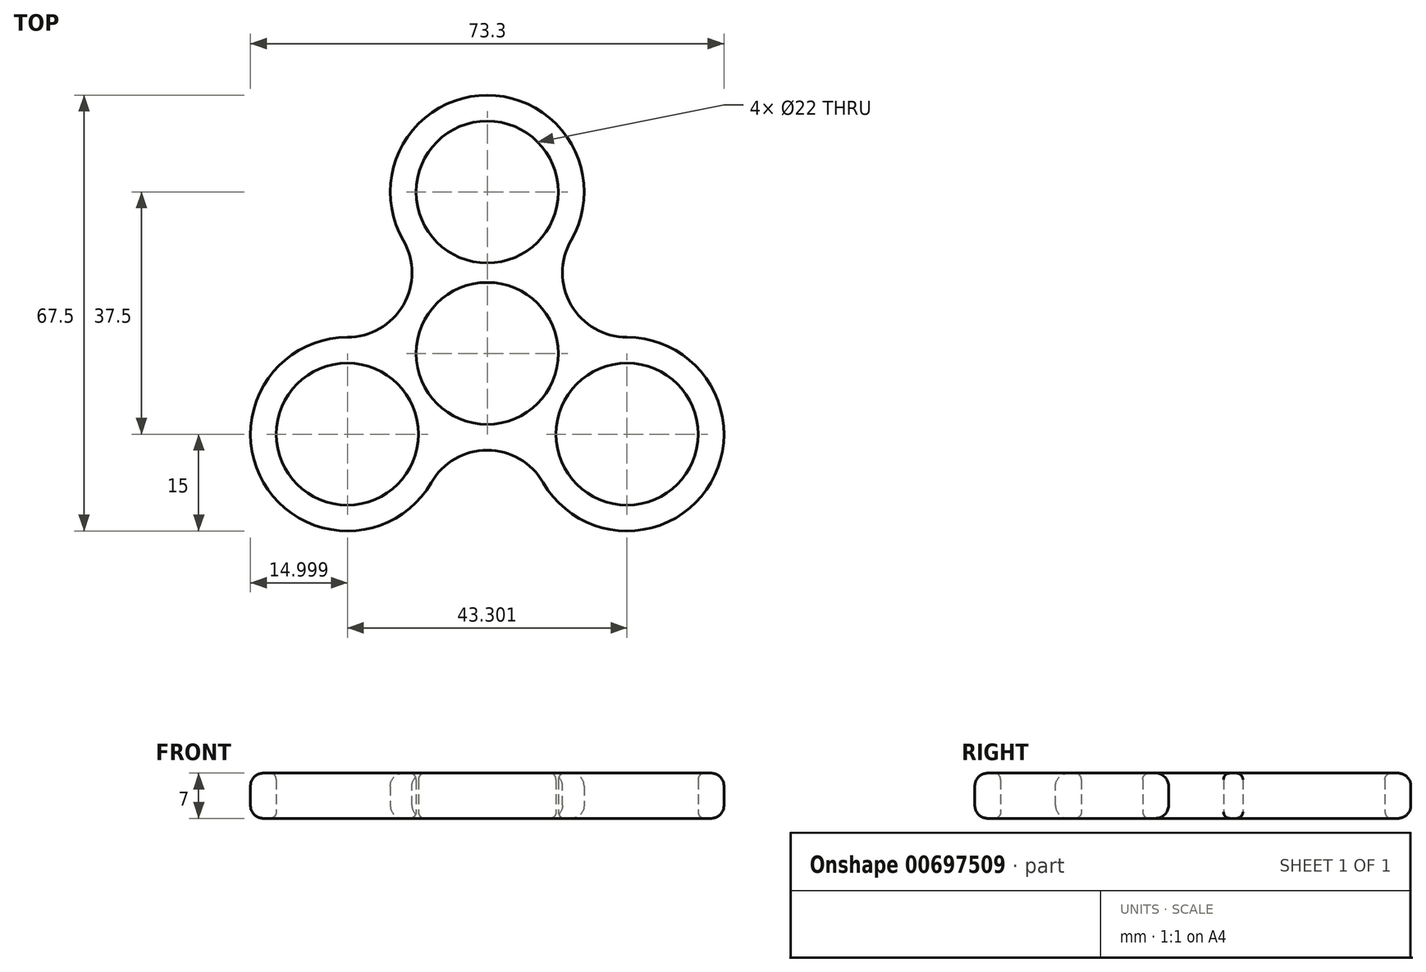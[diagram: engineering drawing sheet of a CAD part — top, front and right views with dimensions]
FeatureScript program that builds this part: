
annotation { "Feature Type Name" : "Feature", "Feature Type Description" : "" }
export const myFeature = defineFeature(function(context is Context, id is Id, definition is map)
    precondition{}
    {
        {
            var Q0;
            Q0=qCreatedBy(makeId("Top.planeOp"),FACE);
            var sketch = newSketch(context, id + "F0", { "sketchPlane" : qUnion([Q0])});
            skCircle(sketch, "E0", {"center": v(0, 0) * mm, "radius": 11 * mm});
            skArc(sketch, "E1", {"start": v(-8.3, 12.5) * mm, "mid": v(-13, 7.5) * mm, "end": v(-14.97, 0.93) * mm});
            skCircle(sketch, "E2", {"center": v(0, 0) * mm, "radius": 25 * mm, "construction": true});
            skLineSegment(sketch, "E3", {"start": v(0, 0) * mm, "end": v(0, 25) * mm, "construction": true});
            skLineSegment(sketch, "E4", {"start": v(0, 0) * mm, "end": v(21.65, -12.5) * mm, "construction": true});
            skLineSegment(sketch, "E5", {"start": v(0, 0) * mm, "end": v(-21.65, -12.5) * mm, "construction": true});
            skCircle(sketch, "E6", {"center": v(0, 25) * mm, "radius": 11 * mm});
            skCircle(sketch, "E7", {"center": v(-21.65, -12.5) * mm, "radius": 11 * mm});
            skArc(sketch, "E8", {"start": v(-14.97, 0.93) * mm, "mid": v(-34.64, -20) * mm, "end": v(-6.68, -13.43) * mm});
            skCircle(sketch, "E9", {"center": v(21.65, -12.5) * mm, "radius": 11 * mm});
            skArc(sketch, "E10", {"start": v(6.68, -13.43) * mm, "mid": v(34.64, -20) * mm, "end": v(14.97, 0.93) * mm});
            skArc(sketch, "E11.trimOffspring", {"start": v(8.3, 12.5) * mm, "mid": v(0, 40) * mm, "end": v(-8.3, 12.5) * mm});
            skArc(sketch, "E12.trimOffspring", {"start": v(-6.68, -13.43) * mm, "mid": v(0, -15) * mm, "end": v(6.68, -13.43) * mm});
            skArc(sketch, "E13.trimOffspring", {"start": v(14.97, 0.93) * mm, "mid": v(13, 7.5) * mm, "end": v(8.3, 12.5) * mm});
            skSolve(sketch);
        }
        {
            var Q0;
            Q0=makeQuery(id+"F0.imprint","IMPRINT",FACE,{"disambiguationData":[TD([[makeQuery(id+"F0.imprint","IMPRINT",EDGE,{"derivedFrom":sQuery(id+"F0.wireOp",EDGE,"E0")}),-1.0]])]});
            extrude(context, id + "F1", {"entities" : qUnion([Q0]), "depth" : 7 * mm, "offsetDistance" : 25 * mm});
        }
        {
            var Q0;
            Q0=makeQuery(id+"F1.opExtrude","SWEPT_EDGE",EDGE,{"disambiguationData":[OSD([sQuery(id+"F0.wireOp",EDGE,"E11.trimOffspring"),sQuery(id+"F0.wireOp",EDGE,"E13.trimOffspring")])]});
            var Q1;
            Q1=makeQuery(id+"F1.opExtrude","SWEPT_EDGE",EDGE,{"disambiguationData":[OSD([sQuery(id+"F0.wireOp",EDGE,"E10"),sQuery(id+"F0.wireOp",EDGE,"E13.trimOffspring")])]});
            var Q2;
            Q2=makeQuery(id+"F1.opExtrude","SWEPT_EDGE",EDGE,{"disambiguationData":[OSD([sQuery(id+"F0.wireOp",EDGE,"E8"),sQuery(id+"F0.wireOp",EDGE,"E12.trimOffspring")])]});
            var Q3;
            Q3=makeQuery(id+"F1.opExtrude","SWEPT_EDGE",EDGE,{"disambiguationData":[OSD([sQuery(id+"F0.wireOp",EDGE,"E10"),sQuery(id+"F0.wireOp",EDGE,"E12.trimOffspring")])]});
            var Q4;
            Q4=makeQuery(id+"F1.opExtrude","SWEPT_EDGE",EDGE,{"disambiguationData":[OSD([sQuery(id+"F0.wireOp",EDGE,"E1"),sQuery(id+"F0.wireOp",EDGE,"E11.trimOffspring")])]});
            var Q5;
            Q5=makeQuery(id+"F1.opExtrude","SWEPT_EDGE",EDGE,{"disambiguationData":[OSD([sQuery(id+"F0.wireOp",EDGE,"E1"),sQuery(id+"F0.wireOp",EDGE,"E8")])]});
            fillet(context, id + "F2", {"entities" : qUnion([Q0, Q1, Q2, Q3, Q4, Q5]), "radius" : 10 * mm, "tangentPropagation" : true, "allowEdgeOverflow" : false});
        }
        {
            var Q0;
            Q0=makeQuery(id+"F1.opExtrude","CAP_EDGE",EDGE,{"disambiguationData":[OSD([sQuery(id+"F0.wireOp",EDGE,"E8")])],"isStart":true});
            var Q1;
            {var subQ0=sQuery(id+"F0.wireOp",EDGE,"E11.trimOffspring");var subQ1=sQuery(id+"F0.wireOp",EDGE,"E1");Q1=makeQuery(id+"F2.opFillet","BLEND_EDGE",EDGE,{"blendedFrom":[makeQuery(id+"F1.opExtrude","SWEPT_EDGE",EDGE,{"disambiguationData":[OSD([subQ1,subQ0])]}),makeQuery(id+"F1.opExtrude","CAP_FACE",FACE,{"disambiguationData":[OSD([sQuery(id+"F0.wireOp",EDGE,"E0"),subQ1,sQuery(id+"F0.wireOp",EDGE,"E6"),sQuery(id+"F0.wireOp",EDGE,"E7"),sQuery(id+"F0.wireOp",EDGE,"E8"),sQuery(id+"F0.wireOp",EDGE,"E9"),sQuery(id+"F0.wireOp",EDGE,"E10"),subQ0,sQuery(id+"F0.wireOp",EDGE,"E12.trimOffspring"),sQuery(id+"F0.wireOp",EDGE,"E13.trimOffspring")])],"isStart":false})],"blendedInto":[makeQuery(id+"F1.opExtrude","CAP_FACE",FACE,{"disambiguationData":[OSD([sQuery(id+"F0.wireOp",EDGE,"E0"),subQ1,sQuery(id+"F0.wireOp",EDGE,"E6"),sQuery(id+"F0.wireOp",EDGE,"E7"),sQuery(id+"F0.wireOp",EDGE,"E8"),sQuery(id+"F0.wireOp",EDGE,"E9"),sQuery(id+"F0.wireOp",EDGE,"E10"),subQ0,sQuery(id+"F0.wireOp",EDGE,"E12.trimOffspring"),sQuery(id+"F0.wireOp",EDGE,"E13.trimOffspring")])],"isStart":false})]});}
            fillet(context, id + "F3", {"entities" : qUnion([Q0, Q1]), "radius" : 2 * mm, "tangentPropagation" : true, "allowEdgeOverflow" : false});
        }
        {
            var Q0;
            Q0=makeQuery(id+"F1.opExtrude","CAP_EDGE",EDGE,{"disambiguationData":[OSD([sQuery(id+"F0.wireOp",EDGE,"E9")])],"isStart":false});
            var Q1;
            Q1=makeQuery(id+"F1.opExtrude","CAP_EDGE",EDGE,{"disambiguationData":[OSD([sQuery(id+"F0.wireOp",EDGE,"E0")])],"isStart":false});
            var Q2;
            Q2=makeQuery(id+"F1.opExtrude","CAP_EDGE",EDGE,{"disambiguationData":[OSD([sQuery(id+"F0.wireOp",EDGE,"E7")])],"isStart":false});
            var Q3;
            Q3=makeQuery(id+"F1.opExtrude","CAP_EDGE",EDGE,{"disambiguationData":[OSD([sQuery(id+"F0.wireOp",EDGE,"E6")])],"isStart":false});
            var Q4;
            Q4=makeQuery(id+"F1.opExtrude","CAP_EDGE",EDGE,{"disambiguationData":[OSD([sQuery(id+"F0.wireOp",EDGE,"E7")])],"isStart":true});
            var Q5;
            Q5=makeQuery(id+"F1.opExtrude","CAP_EDGE",EDGE,{"disambiguationData":[OSD([sQuery(id+"F0.wireOp",EDGE,"E9")])],"isStart":true});
            var Q6;
            Q6=makeQuery(id+"F1.opExtrude","CAP_EDGE",EDGE,{"disambiguationData":[OSD([sQuery(id+"F0.wireOp",EDGE,"E0")])],"isStart":true});
            var Q7;
            Q7=makeQuery(id+"F1.opExtrude","CAP_EDGE",EDGE,{"disambiguationData":[OSD([sQuery(id+"F0.wireOp",EDGE,"E6")])],"isStart":true});
            fillet(context, id + "F4", {"entities" : qUnion([Q0, Q1, Q2, Q3, Q4, Q5, Q6, Q7]), "radius" : 1 * mm, "tangentPropagation" : true, "allowEdgeOverflow" : false});
        }
    });
